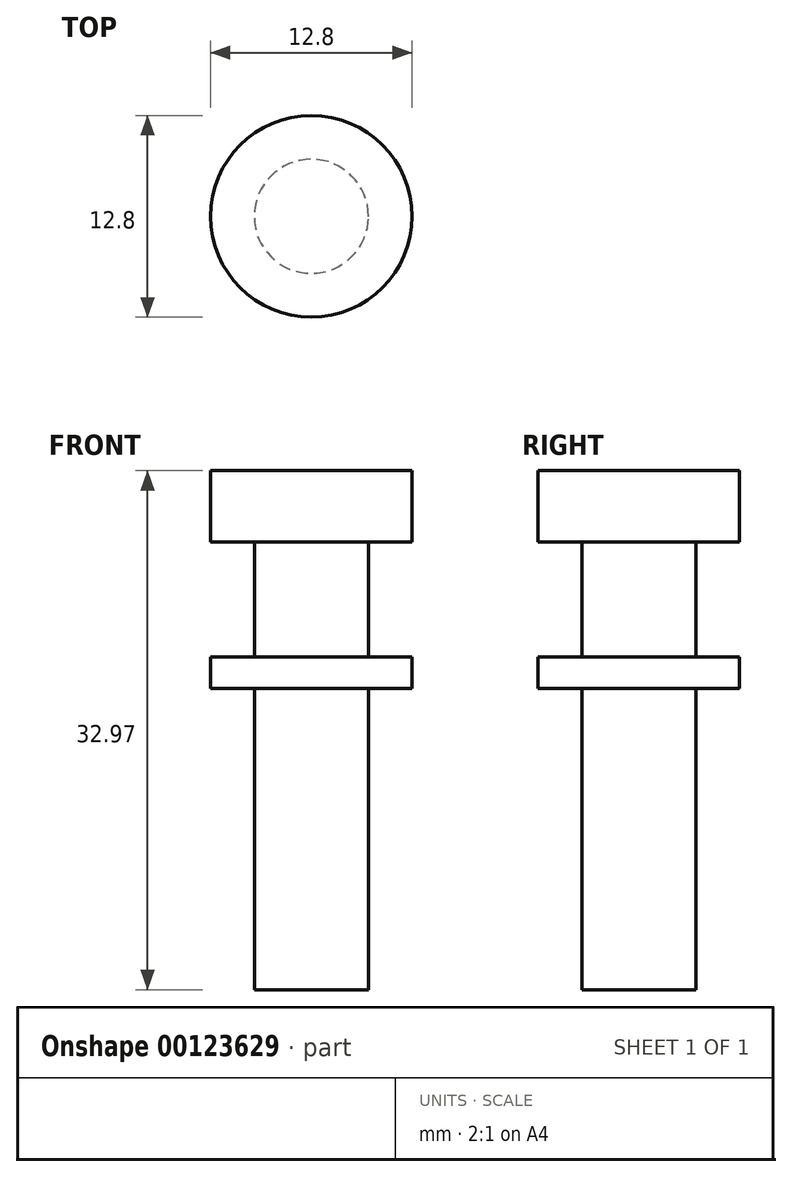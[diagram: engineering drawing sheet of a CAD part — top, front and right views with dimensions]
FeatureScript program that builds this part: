
annotation { "Feature Type Name" : "Feature", "Feature Type Description" : "" }
export const myFeature = defineFeature(function(context is Context, id is Id, definition is map)
    precondition{}
    {
        {
            var Q0;
            Q0=qCreatedBy(makeId("Top.planeOp"),FACE);
            var sketch = newSketch(context, id + "F0", { "sketchPlane" : qUnion([Q0])});
            skCircle(sketch, "E0", {"center": v(0, 0) * mm, "radius": 3.63 * mm});
            skSolve(sketch);
        }
        {
            var Q0;
            Q0 = qSketchRegion(id + "F0", true);
            extrude(context, id + "F1", {"entities" : qUnion([Q0]), "depth" : 7.3 * mm});
        }
        {
            var Q0;
            Q0=makeQuery(id+"F1.opExtrude","CAP_FACE",FACE,{"disambiguationData":[OSD([sQuery(id+"F0.wireOp",EDGE,"E0")])],"isStart":false});
            var sketch = newSketch(context, id + "F2", { "sketchPlane" : qUnion([Q0])});
            skCircle(sketch, "E1", {"center": v(0, 0) * mm, "radius": 6.4 * mm});
            skSolve(sketch);
        }
        {
            var Q0;
            Q0 = qSketchRegion(id + "F2", true);
            var Q1;
            Q1=makeQuery(id+"F2.imprint","IMPRINT",FACE,{"disambiguationData":[TD([[makeQuery(id+"F2.imprint","IMPRINT",EDGE,{"derivedFrom":sQuery(id+"F2.wireOp",EDGE,"E1")}),1.0]])]});
            extrude(context, id + "F3", {"entities" : qUnion([Q0, Q1]), "operationType" : NewBodyOperationType.ADD, "depth" : 4.55 * mm});
        }
        {
            var Q0;
            Q0=makeQuery(id+"F1.opExtrude","CAP_FACE",FACE,{"disambiguationData":[OSD([sQuery(id+"F0.wireOp",EDGE,"E0")])],"isStart":true});
            var sketch = newSketch(context, id + "F4", { "sketchPlane" : qUnion([Q0])});
            skCircle(sketch, "E2", {"center": v(0, 0) * mm, "radius": 6.4 * mm});
            skSolve(sketch);
        }
        {
            var Q0;
            Q0 = qSketchRegion(id + "F4", true);
            extrude(context, id + "F5", {"entities" : qUnion([Q0]), "operationType" : NewBodyOperationType.ADD, "depth" : 2 * mm});
        }
        {
            var Q0;
            Q0=makeQuery(id+"F5.opExtrude","CAP_FACE",FACE,{"disambiguationData":[OSD([sQuery(id+"F4.wireOp",EDGE,"E2")])],"isStart":false});
            var sketch = newSketch(context, id + "F6", { "sketchPlane" : qUnion([Q0])});
            skCircle(sketch, "E3", {"center": v(0, 0) * mm, "radius": 3.62 * mm});
            skSolve(sketch);
        }
        {
            var Q0;
            Q0=makeQuery(id+"F6.imprint","IMPRINT",FACE,{"disambiguationData":[TD([[makeQuery(id+"F6.imprint","IMPRINT",EDGE,{"derivedFrom":sQuery(id+"F6.wireOp",EDGE,"E3")}),1.0]])]});
            extrude(context, id + "F7", {"entities" : qUnion([Q0]), "operationType" : NewBodyOperationType.ADD, "depth" : 19.12 * mm});
        }
    });
